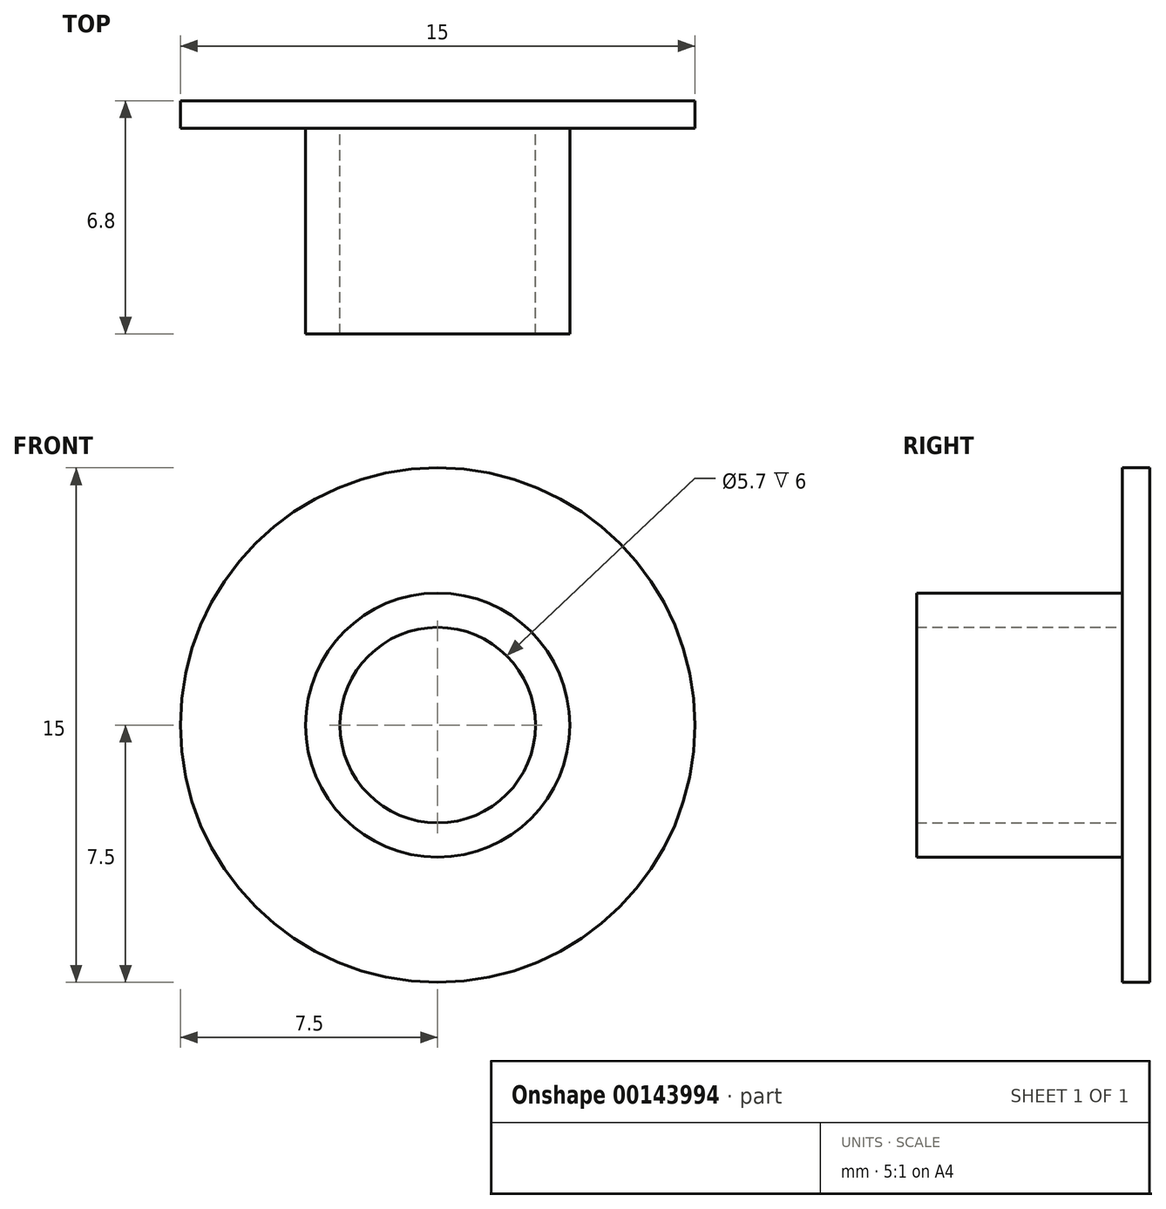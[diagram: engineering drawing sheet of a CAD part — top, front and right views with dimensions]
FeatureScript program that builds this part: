
annotation { "Feature Type Name" : "Feature", "Feature Type Description" : "" }
export const myFeature = defineFeature(function(context is Context, id is Id, definition is map)
    precondition{}
    {
        {
            var Q0;
            Q0=qCreatedBy(makeId("Front.planeOp"),FACE);
            var sketch = newSketch(context, id + "F0", { "sketchPlane" : qUnion([Q0])});
            skCircle(sketch, "E0", {"center": v(0, 0) * mm, "radius": 7.5 * mm});
            skSolve(sketch);
        }
        {
            var Q0;
            Q0=makeQuery(id+"F0.imprint","IMPRINT",FACE,{"disambiguationData":[TD([[makeQuery(id+"F0.imprint","IMPRINT",EDGE,{"derivedFrom":sQuery(id+"F0.wireOp",EDGE,"E0")}),1.0]])]});
            extrude(context, id + "F1", {"entities" : qUnion([Q0]), "depth" : 0.8 * mm});
        }
        {
            var Q0;
            Q0=makeQuery(id+"F1.opExtrude","CAP_FACE",FACE,{"disambiguationData":[OSD([sQuery(id+"F0.wireOp",EDGE,"E0")])],"isStart":false});
            var sketch = newSketch(context, id + "F2", { "sketchPlane" : qUnion([Q0])});
            skSolve(sketch);
        }
        {
            var Q0;
            Q0=makeQuery(id+"F2.imprint","IMPRINT",FACE,{"disambiguationData":[TD([[makeQuery(id+"F2.imprint","IMPRINT",EDGE,{"derivedFrom":makeQuery(id+"F1.opExtrude","CAP_EDGE",EDGE,{"disambiguationData":[OSD([sQuery(id+"F0.wireOp",EDGE,"E0")])],"isStart":false})}),1.0]])]});
            var sketch = newSketch(context, id + "F3", { "sketchPlane" : qUnion([Q0])});
            skCircle(sketch, "E1", {"center": v(0, 0) * mm, "radius": 2.85 * mm});
            skCircle(sketch, "E2.0", {"center": v(0, 0) * mm, "radius": 3.85 * mm});
            skSolve(sketch);
        }
        {
            var Q0;
            Q0=qSketchRegion(id+"F3",true);
            extrude(context, id + "F4", {"entities" : qUnion([Q0]), "operationType" : NewBodyOperationType.ADD, "depth" : 6 * mm});
        }
    });
